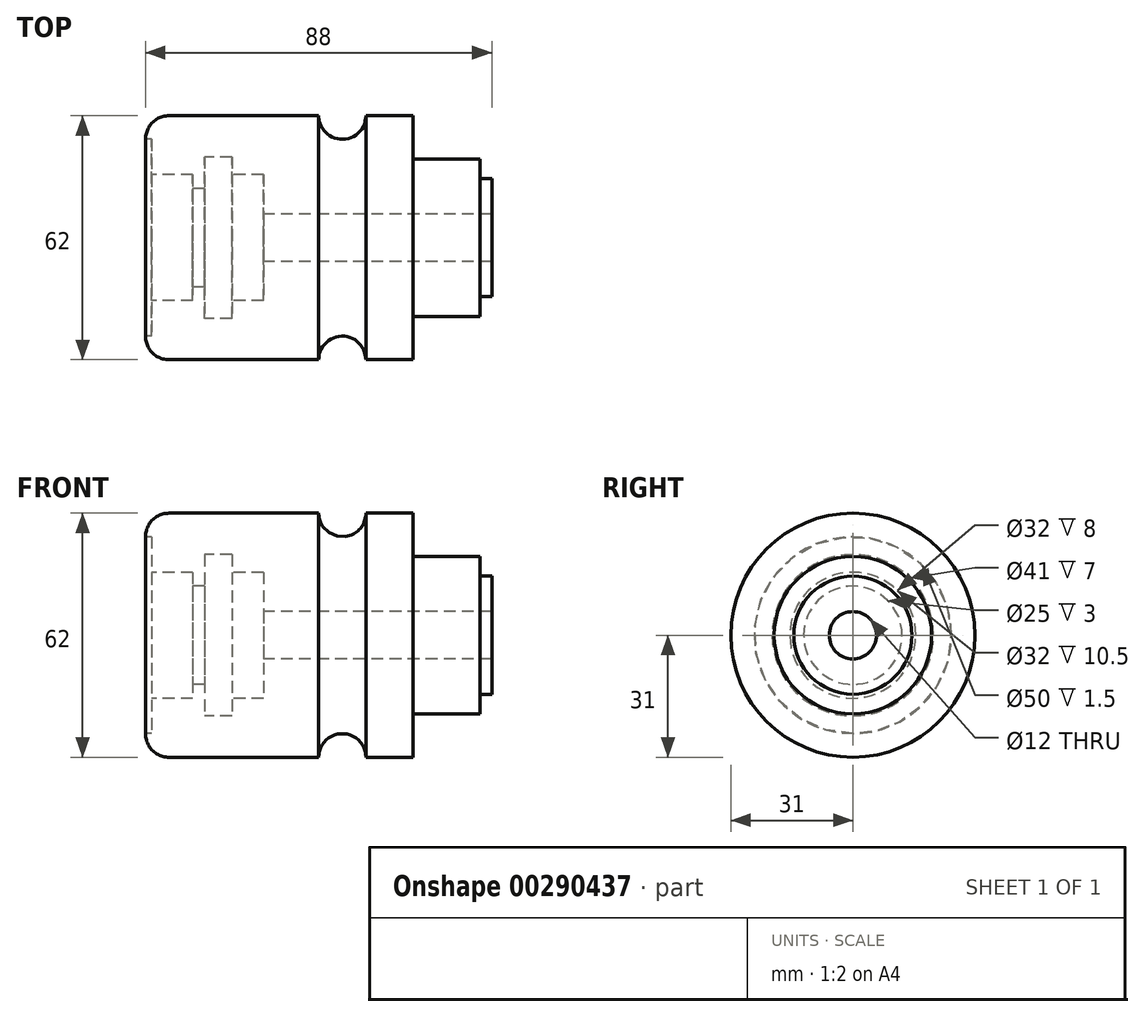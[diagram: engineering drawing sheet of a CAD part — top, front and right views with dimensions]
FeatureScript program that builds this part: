
annotation { "Feature Type Name" : "Feature", "Feature Type Description" : "" }
export const myFeature = defineFeature(function(context is Context, id is Id, definition is map)
    precondition{}
    {
        {
            var Q0;
            Q0=qCreatedBy(makeId("Front.planeOp"),FACE);
            var sketch = newSketch(context, id + "F0", { "sketchPlane" : qUnion([Q0])});
            skLineSegment(sketch, "E0", {"start": v(0, 0) * mm, "end": v(0, 25) * mm});
            skLineSegment(sketch, "E1", {"start": v(0, 25) * mm, "end": v(1.5, 25) * mm});
            skLineSegment(sketch, "E2", {"start": v(1.5, 25) * mm, "end": v(1.5, 16) * mm});
            skLineSegment(sketch, "E3", {"start": v(1.5, 16) * mm, "end": v(12, 16) * mm});
            skLineSegment(sketch, "E4", {"start": v(12, 16) * mm, "end": v(12, 12.5) * mm});
            skLineSegment(sketch, "E5", {"start": v(12, 12.5) * mm, "end": v(15, 12.5) * mm});
            skLineSegment(sketch, "E6", {"start": v(22, 16) * mm, "end": v(30, 16) * mm});
            skLineSegment(sketch, "E7", {"start": v(30, 16) * mm, "end": v(30, 6) * mm});
            skLineSegment(sketch, "E8", {"start": v(30, 6) * mm, "end": v(88, 6) * mm});
            skLineSegment(sketch, "E9", {"start": v(88, 6) * mm, "end": v(88, 0) * mm});
            skLineSegment(sketch, "E10", {"start": v(88, 0) * mm, "end": v(0, 0) * mm});
            skLineSegment(sketch, "E11", {"start": v(0, 0) * mm, "end": v(-22.5, 0) * mm, "construction": true});
            skLineSegment(sketch, "E12", {"start": v(15, 12.5) * mm, "end": v(15, 20.5) * mm});
            skLineSegment(sketch, "E13", {"start": v(15, 20.5) * mm, "end": v(22, 20.5) * mm});
            skLineSegment(sketch, "E14", {"start": v(22, 20.5) * mm, "end": v(22, 16) * mm});
            skSolve(sketch);
        }
        {
            var Q0;
            Q0=qCreatedBy(makeId("Front.planeOp"),FACE);
            var sketch = newSketch(context, id + "F1", { "sketchPlane" : qUnion([Q0])});
            skLineSegment(sketch, "E15", {"start": v(0, 0) * mm, "end": v(96.17, 0) * mm, "construction": true});
            skLineSegment(sketch, "E16", {"start": v(0, 0) * mm, "end": v(0, 31) * mm, "construction": true});
            skLineSegment(sketch, "E17", {"start": v(0, 31) * mm, "end": v(44, 31) * mm});
            skLineSegment(sketch, "E18", {"start": v(68, 31) * mm, "end": v(68, 20) * mm});
            skLineSegment(sketch, "E19", {"start": v(68, 20) * mm, "end": v(85, 20) * mm});
            skLineSegment(sketch, "E20", {"start": v(85, 20) * mm, "end": v(85, 15) * mm});
            skLineSegment(sketch, "E21", {"start": v(85, 15) * mm, "end": v(88, 15) * mm});
            skLineSegment(sketch, "E22", {"start": v(88, 15) * mm, "end": v(88, 0) * mm});
            skArc(sketch, "E23", {"start": v(44, 31) * mm, "mid": v(50, 25) * mm, "end": v(56, 31) * mm});
            skLineSegment(sketch, "E24.trimOffspring", {"start": v(56, 31) * mm, "end": v(68, 31) * mm});
            skLineSegment(sketch, "E25", {"start": v(96.17, 0) * mm, "end": v(0, 0) * mm});
            skLineSegment(sketch, "E26", {"start": v(0, 31) * mm, "end": v(0, 0) * mm});
            skSolve(sketch);
        }
        {
            var Q0;
            Q0 = qSketchRegion(id + "F1", true);
            var Q1;
            Q1=sQuery(id+"F1.wireOp",EDGE,"E25");
            revolve(context, id + "F2", {"entities" : qUnion([Q0]), "axis" : qUnion([Q1]), "revolveType" : RevolveType.FULL});
        }
        {
            var Q0;
            Q0 = qSketchRegion(id + "F0", true);
            var Q1;
            Q1=sQuery(id+"F0.wireOp",EDGE,"E11");
            revolve(context, id + "F3", {"operationType" : NewBodyOperationType.REMOVE, "entities" : qUnion([Q0]), "axis" : qUnion([Q1]), "revolveType" : RevolveType.FULL, "oppositeDirection" : true});
        }
        {
            var Q0;
            Q0=makeQuery(id+"F2.opRevolve","SWEPT_EDGE",EDGE,{"disambiguationData":[OSD([sQuery(id+"F1.wireOp",EDGE,"E17"),sQuery(id+"F1.wireOp",EDGE,"E26")])]});
            fillet(context, id + "F4", {"entities" : qUnion([Q0]), "radius" : 6 * mm, "tangentPropagation" : true, "allowEdgeOverflow" : false});
        }
    });
